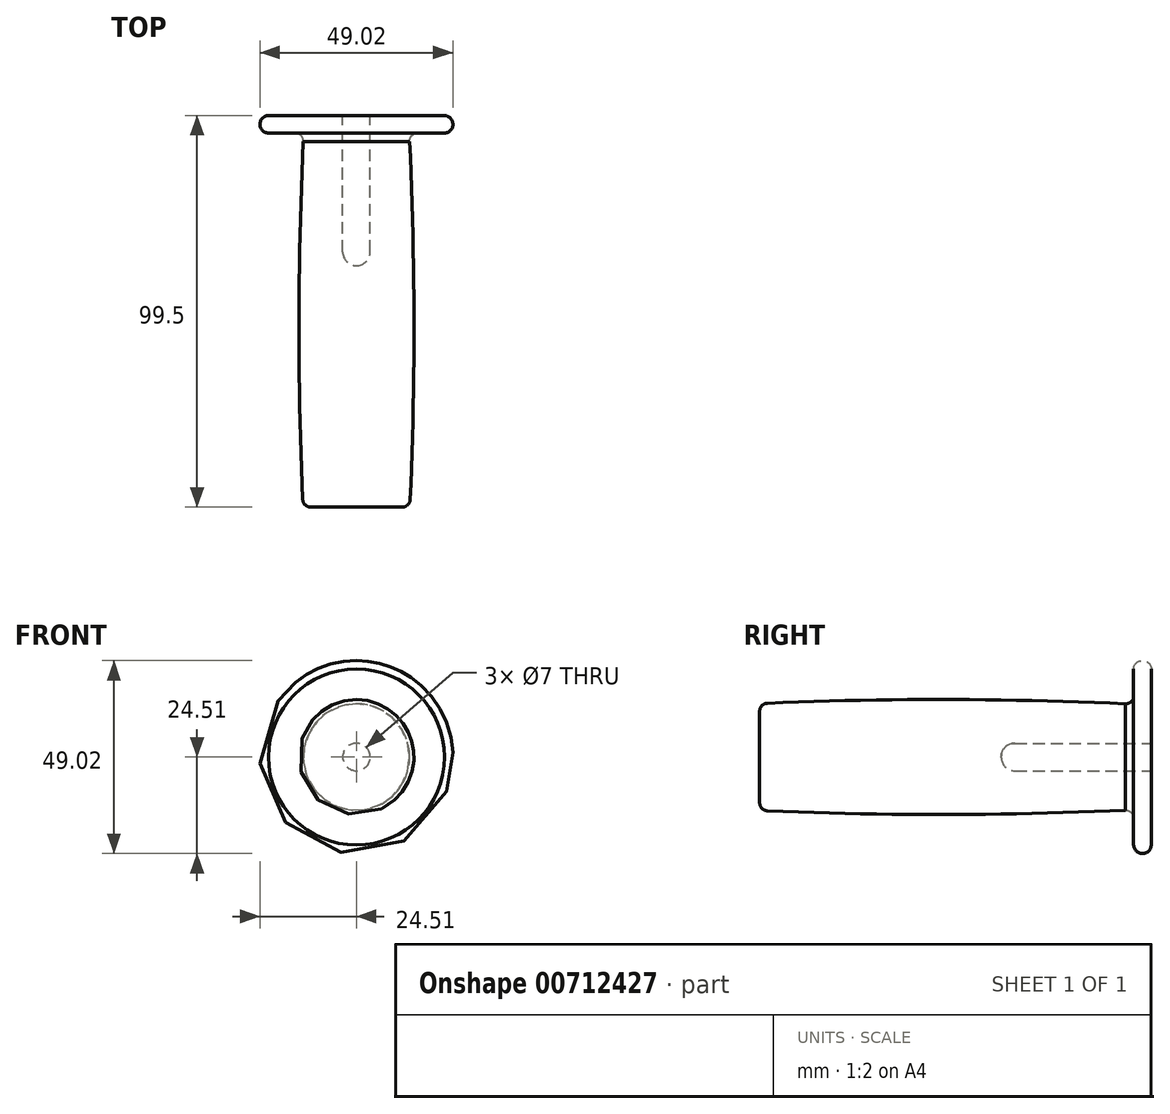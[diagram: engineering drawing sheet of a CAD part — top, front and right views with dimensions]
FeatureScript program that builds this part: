
annotation { "Feature Type Name" : "Feature", "Feature Type Description" : "" }
export const myFeature = defineFeature(function(context is Context, id is Id, definition is map)
    precondition{}
    {
        {
            var Q0;
            Q0=qCreatedBy(makeId("Right.planeOp"),FACE);
            var sketch = newSketch(context, id + "F0", { "sketchPlane" : qUnion([Q0])});
            skLineSegment(sketch, "E0", {"start": v(18.73, 0) * mm, "end": v(-137.75, 0) * mm, "construction": true});
            skPoint(sketch, "E1.orphan", {"position": v(-108.9, -19.6) * mm});
            skLineSegment(sketch, "E2", {"start": v(-4.5, 15.51) * mm, "end": v(-4.5, 22.37) * mm});
            skArc(sketch, "E3", {"start": v(0, 22.37) * mm, "mid": v(-2.25, 24.5) * mm, "end": v(-4.5, 22.37) * mm});
            skLineSegment(sketch, "E4", {"start": v(0, 22.37) * mm, "end": v(0, 0) * mm});
            skPoint(sketch, "E5.visualSharp", {"position": v(-4.5, 14.26) * mm});
            skArc(sketch, "E5.filletArc", {"start": v(-6.62, 13.52) * mm, "mid": v(-5.13, 14.06) * mm, "end": v(-4.5, 15.51) * mm});
            skLineSegment(sketch, "E6", {"start": v(0, 3.5) * mm, "end": v(-34.66, 3.5) * mm});
            skLineSegment(sketch, "E7", {"start": v(-38.16, 0) * mm, "end": v(-38.16, 0) * mm});
            skLineSegment(sketch, "E8", {"start": v(-110.23, 0) * mm, "end": v(-38.16, 0) * mm});
            skPoint(sketch, "E9.visualSharp", {"position": v(-38.16, 3.5) * mm});
            skArc(sketch, "E9.filletArc", {"start": v(-34.66, 3.5) * mm, "mid": v(-37.14, 2.47) * mm, "end": v(-38.16, 0) * mm});
            skLineSegment(sketch, "E10", {"start": v(-9.5, 21.24) * mm, "end": v(-9.5, 0) * mm, "construction": true});
            skLineSegment(sketch, "E11", {"start": v(-99.5, 18.81) * mm, "end": v(-99.5, 0) * mm, "construction": true});
            skLineSegment(sketch, "E12", {"start": v(-101.64, 12) * mm, "end": v(-6.68, 12) * mm, "construction": true});
            skLineSegment(sketch, "E13", {"start": v(-99.5, 12) * mm, "end": v(-99.5, 15.14) * mm});
            skArc(sketch, "E14", {"start": v(-6.62, 13.52) * mm, "mid": v(-52.1, 14.6) * mm, "end": v(-97.59, 13.65) * mm});
            skLineSegment(sketch, "E15", {"start": v(-99.5, 11.66) * mm, "end": v(-99.5, 0) * mm});
            skPoint(sketch, "E16.visualSharp", {"position": v(-99.5, 13.57) * mm});
            skArc(sketch, "E16.filletArc", {"start": v(-97.59, 13.65) * mm, "mid": v(-98.94, 13.04) * mm, "end": v(-99.5, 11.66) * mm});
            skSolve(sketch);
        }
        {
            var Q0;
            Q0=makeQuery(id+"F0.imprint","IMPRINT",FACE,{"disambiguationData":[TD([[makeQuery(id+"F0.imprint","IMPRINT",EDGE,{"derivedFrom":sQuery(id+"F0.wireOp",EDGE,"72d4449f-fd17-47fe-a6cc-5c9fe78215aa")}),-1.0]])]});
            var Q1;
            Q1=makeQuery(id+"F0.imprint","IMPRINT",FACE,{"disambiguationData":[TD([[makeQuery(id+"F0.imprint","IMPRINT",EDGE,{"derivedFrom":sQuery(id+"F0.wireOp",EDGE,"E2")}),-1.0]])]});
            var Q2;
            Q2=sQuery(id+"F0.wireOp",EDGE,"E0");
            revolve(context, id + "F1", {"entities" : qUnion([Q0, Q1]), "axis" : qUnion([Q2]), "revolveType" : RevolveType.FULL, "surfaceOperationType" : NewSurfaceOperationType.NEW});
        }
    });
